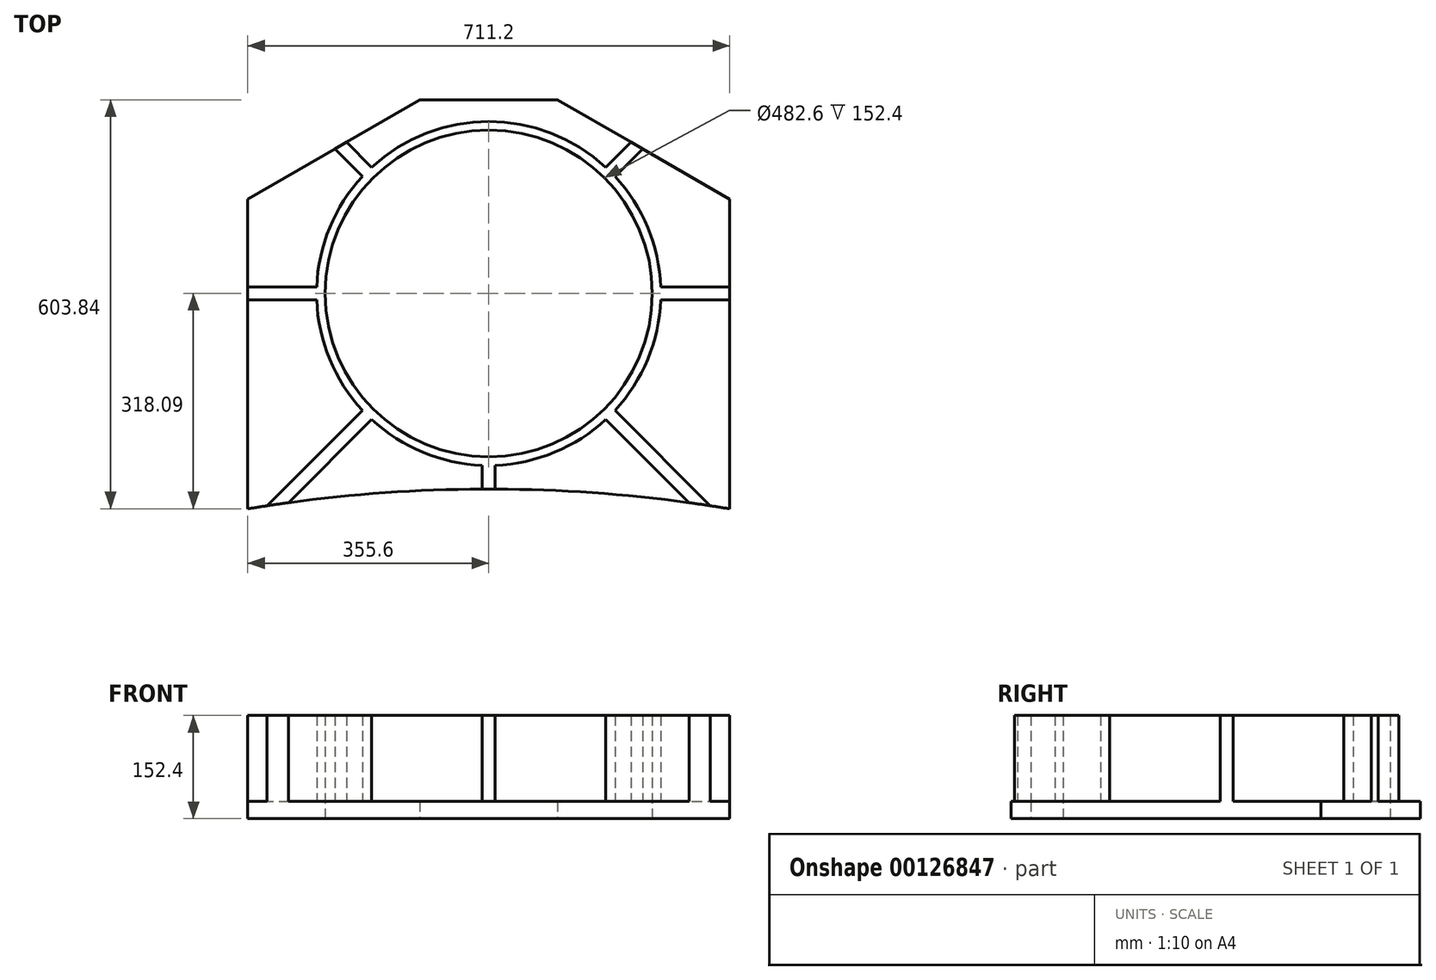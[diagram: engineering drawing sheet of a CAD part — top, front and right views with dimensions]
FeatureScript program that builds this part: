
annotation { "Feature Type Name" : "Feature", "Feature Type Description" : "" }
export const myFeature = defineFeature(function(context is Context, id is Id, definition is map)
    precondition{}
    {
        {
            var Q0;
            Q0=qCreatedBy(makeId("Top.planeOp"),FACE);
            var sketch = newSketch(context, id + "F0", { "sketchPlane" : qUnion([Q0])});
            skLineSegment(sketch, "E0", {"start": v(0, 433.67) * mm, "end": v(0, -509.33) * mm, "construction": true});
            skLineSegment(sketch, "E1", {"start": v(-670.07, 0) * mm, "end": v(724.11, 0) * mm, "construction": true});
            skPoint(sketch, "E2", {"position": v(-101.6, 285.75) * mm});
            skPoint(sketch, "E3", {"position": v(0, 401.5) * mm});
            skPoint(sketch, "E4", {"position": v(101.6, 285.75) * mm});
            skPoint(sketch, "E5", {"position": v(-355.6, 139.1) * mm});
            skPoint(sketch, "E6", {"position": v(355.6, 139.1) * mm});
            skPoint(sketch, "E7", {"position": v(-355.6, -318.09) * mm});
            skArc(sketch, "E8", {"start": v(-355.6, -318.09) * mm, "mid": v(0, -288.92) * mm, "end": v(355.6, -318.09) * mm});
            skLineSegment(sketch, "E9", {"start": v(-355.6, -318.09) * mm, "end": v(-355.6, 139.1) * mm});
            skLineSegment(sketch, "E10", {"start": v(-355.6, 139.1) * mm, "end": v(-101.6, 285.75) * mm});
            skLineSegment(sketch, "E11", {"start": v(-101.6, 285.75) * mm, "end": v(101.6, 285.75) * mm});
            skLineSegment(sketch, "E12", {"start": v(101.6, 285.75) * mm, "end": v(355.6, 139.1) * mm});
            skLineSegment(sketch, "E13", {"start": v(355.6, 139.1) * mm, "end": v(355.6, -318.09) * mm});
            skSolve(sketch);
        }
        {
            var Q0;
            Q0 = qSketchRegion(id + "F0", true);
            extrude(context, id + "F1", {"entities" : qUnion([Q0]), "depth" : 25.4 * mm});
        }
        {
            var Q0;
            Q0=makeQuery(id+"F1.opExtrude","CAP_FACE",FACE,{"disambiguationData":[OSD([sQuery(id+"F0.wireOp",EDGE,"E8"),sQuery(id+"F0.wireOp",EDGE,"E9"),sQuery(id+"F0.wireOp",EDGE,"E10"),sQuery(id+"F0.wireOp",EDGE,"E11"),sQuery(id+"F0.wireOp",EDGE,"E12"),sQuery(id+"F0.wireOp",EDGE,"E13")])],"isStart":false});
            var sketch = newSketch(context, id + "F2", { "sketchPlane" : qUnion([Q0])});
            skLineSegment(sketch, "E14", {"start": v(0, 309.88) * mm, "end": v(0, -342.34) * mm, "construction": true});
            skPoint(sketch, "E14.startSnap0", {"position": v(0, 285.75) * mm});
            skLineSegment(sketch, "E15", {"start": v(-399.29, 0) * mm, "end": v(392.69, 0) * mm, "construction": true});
            skLineSegment(sketch, "E16", {"start": v(-257.96, 257.96) * mm, "end": v(384.23, -384.23) * mm, "construction": true});
            skLineSegment(sketch, "E17", {"start": v(-377.64, -377.64) * mm, "end": v(275.76, 275.76) * mm, "construction": true});
            skLineSegment(sketch, "E18", {"start": v(-226.89, 213.42) * mm, "end": v(-60.2, 46.72) * mm});
            skLineSegment(sketch, "E19", {"start": v(-209.8, 223.28) * mm, "end": v(-46.72, 60.2) * mm});
            skLineSegment(sketch, "E20", {"start": v(-327.03, -313.56) * mm, "end": v(-60.2, -46.72) * mm});
            skLineSegment(sketch, "E21", {"start": v(-295.56, -309.03) * mm, "end": v(-46.72, -60.2) * mm});
            skLineSegment(sketch, "E22", {"start": v(-355.6, 9.52) * mm, "end": v(-75.6, 9.52) * mm});
            skLineSegment(sketch, "E23", {"start": v(-355.6, -9.53) * mm, "end": v(-75.6, -9.53) * mm});
            skLineSegment(sketch, "E24", {"start": v(-355.6, 139.1) * mm, "end": v(-101.6, 285.75) * mm, "construction": true});
            skLineSegment(sketch, "E25", {"start": v(-101.6, 285.75) * mm, "end": v(101.6, 285.75) * mm, "construction": true});
            skLineSegment(sketch, "E26", {"start": v(101.6, 285.75) * mm, "end": v(355.6, 139.1) * mm, "construction": true});
            skLineSegment(sketch, "E27", {"start": v(355.6, 139.1) * mm, "end": v(355.6, -318.09) * mm, "construction": true});
            skLineSegment(sketch, "E28", {"start": v(-355.6, -318.09) * mm, "end": v(-355.6, 139.1) * mm, "construction": true});
            skArc(sketch, "E29", {"start": v(-355.6, -318.09) * mm, "mid": v(0, -288.92) * mm, "end": v(355.6, -318.09) * mm, "construction": true});
            skLineSegment(sketch, "E30", {"start": v(-355.6, -9.53) * mm, "end": v(-355.6, 9.52) * mm});
            skLineSegment(sketch, "E31", {"start": v(-226.89, 213.42) * mm, "end": v(-209.8, 223.28) * mm});
            skLineSegment(sketch, "E32", {"start": v(209.8, 223.28) * mm, "end": v(226.89, 213.42) * mm});
            skLineSegment(sketch, "E33", {"start": v(355.6, 9.53) * mm, "end": v(355.6, -9.52) * mm});
            skArc(sketch, "E34", {"start": v(-327.03, -313.56) * mm, "mid": v(-311.3, -311.24) * mm, "end": v(-295.56, -309.03) * mm});
            skArc(sketch, "E35", {"start": v(295.56, -309.03) * mm, "mid": v(311.3, -311.24) * mm, "end": v(327.03, -313.56) * mm});
            skLineSegment(sketch, "E36", {"start": v(-9.52, -288.95) * mm, "end": v(9.53, -288.95) * mm});
            skCircle(sketch, "E37", {"center": v(0, 0) * mm, "radius": 76.2 * mm, "construction": true});
            skLineSegment(sketch, "E38.trimOffspring", {"start": v(-9.52, -75.6) * mm, "end": v(-9.52, -288.95) * mm});
            skLineSegment(sketch, "E39.trimOffspring", {"start": v(9.53, -75.6) * mm, "end": v(9.53, -288.95) * mm});
            skLineSegment(sketch, "E40.trimOffspring", {"start": v(46.72, -60.2) * mm, "end": v(295.56, -309.03) * mm});
            skLineSegment(sketch, "E41.trimOffspring", {"start": v(60.2, -46.72) * mm, "end": v(327.03, -313.56) * mm});
            skLineSegment(sketch, "E42.trimOffspring", {"start": v(75.6, -9.52) * mm, "end": v(355.6, -9.52) * mm});
            skLineSegment(sketch, "E43.trimOffspring", {"start": v(75.6, 9.53) * mm, "end": v(355.6, 9.53) * mm});
            skLineSegment(sketch, "E44.trimOffspring", {"start": v(60.2, 46.72) * mm, "end": v(226.89, 213.42) * mm});
            skLineSegment(sketch, "E45.trimOffspring", {"start": v(46.72, 60.2) * mm, "end": v(209.8, 223.28) * mm});
            skArc(sketch, "E46", {"start": v(-60.2, 46.72) * mm, "mid": v(-53.88, 53.88) * mm, "end": v(-46.72, 60.2) * mm});
            skArc(sketch, "E47", {"start": v(46.72, 60.2) * mm, "mid": v(53.88, 53.88) * mm, "end": v(60.2, 46.72) * mm});
            skArc(sketch, "E48", {"start": v(75.6, 9.53) * mm, "mid": v(76.2, 0) * mm, "end": v(75.6, -9.52) * mm});
            skArc(sketch, "E49", {"start": v(60.2, -46.72) * mm, "mid": v(53.88, -53.88) * mm, "end": v(46.72, -60.2) * mm});
            skArc(sketch, "E50", {"start": v(9.53, -75.6) * mm, "mid": v(0, -76.2) * mm, "end": v(-9.52, -75.6) * mm});
            skArc(sketch, "E51", {"start": v(-46.72, -60.2) * mm, "mid": v(-53.88, -53.88) * mm, "end": v(-60.2, -46.72) * mm});
            skArc(sketch, "E52", {"start": v(-75.6, -9.52) * mm, "mid": v(-76.2, 0) * mm, "end": v(-75.6, 9.52) * mm});
            skSolve(sketch);
        }
        {
            var Q0;
            Q0 = qSketchRegion(id + "F2", true);
            extrude(context, id + "F3", {"entities" : qUnion([Q0]), "operationType" : NewBodyOperationType.ADD, "depth" : 127 * mm});
        }
        {
            var Q0;
            Q0=makeQuery(id+"F1.opExtrude","CAP_FACE",FACE,{"disambiguationData":[OSD([sQuery(id+"F0.wireOp",EDGE,"E8"),sQuery(id+"F0.wireOp",EDGE,"E9"),sQuery(id+"F0.wireOp",EDGE,"E10"),sQuery(id+"F0.wireOp",EDGE,"E11"),sQuery(id+"F0.wireOp",EDGE,"E12"),sQuery(id+"F0.wireOp",EDGE,"E13")])],"isStart":true});
            var sketch = newSketch(context, id + "F4", { "sketchPlane" : qUnion([Q0])});
            skCircle(sketch, "E53", {"center": v(0, 0) * mm, "radius": 254 * mm});
            skSolve(sketch);
        }
        {
            var Q0;
            Q0 = qSketchRegion(id + "F4", true);
            var Q1;
            Q1=makeQuery(id+"F3.opExtrude","CAP_FACE",FACE,{"disambiguationData":[OSD([sQuery(id+"F2.wireOp",EDGE,"E22"),sQuery(id+"F2.wireOp",EDGE,"E23"),sQuery(id+"F2.wireOp",EDGE,"E30"),sQuery(id+"F2.wireOp",EDGE,"E52")])],"isStart":false});
            extrude(context, id + "F5", {"entities" : qUnion([Q0]), "operationType" : NewBodyOperationType.ADD, "endBound" : BoundingType.UP_TO_SURFACE, "oppositeDirection" : true, "endBoundEntityFace" : qUnion([Q1]), "depth" : 25.4 * mm});
        }
        {
            var Q0;
            Q0=makeQuery(id+"F1.opExtrude","CAP_FACE",FACE,{"disambiguationData":[OSD([sQuery(id+"F0.wireOp",EDGE,"E8"),sQuery(id+"F0.wireOp",EDGE,"E9"),sQuery(id+"F0.wireOp",EDGE,"E10"),sQuery(id+"F0.wireOp",EDGE,"E11"),sQuery(id+"F0.wireOp",EDGE,"E12"),sQuery(id+"F0.wireOp",EDGE,"E13")])],"isStart":true});
            var sketch = newSketch(context, id + "F6", { "sketchPlane" : qUnion([Q0])});
            skCircle(sketch, "E54", {"center": v(0, 0) * mm, "radius": 241.3 * mm});
            skSolve(sketch);
        }
        {
            var Q0;
            Q0 = qSketchRegion(id + "F6", true);
            var Q1;
            {var subQ0=sQuery(id+"F2.wireOp",EDGE,"E52");var subQ1=sQuery(id+"F2.wireOp",EDGE,"E30");var subQ2=sQuery(id+"F2.wireOp",EDGE,"E23");var subQ3=sQuery(id+"F2.wireOp",EDGE,"E22");Q1=makeQuery(id+"F5.boolean.opBoolean","MERGE",FACE,{"derivedFrom":[makeQuery(id+"F3.opExtrude","CAP_FACE",FACE,{"disambiguationData":[OSD([sQuery(id+"F2.wireOp",EDGE,"E18"),sQuery(id+"F2.wireOp",EDGE,"E19"),sQuery(id+"F2.wireOp",EDGE,"E31"),sQuery(id+"F2.wireOp",EDGE,"E46")])],"isStart":false}),makeQuery(id+"F3.opExtrude","CAP_FACE",FACE,{"disambiguationData":[OSD([sQuery(id+"F2.wireOp",EDGE,"E20"),sQuery(id+"F2.wireOp",EDGE,"E21"),sQuery(id+"F2.wireOp",EDGE,"E34"),sQuery(id+"F2.wireOp",EDGE,"E51")])],"isStart":false}),makeQuery(id+"F3.opExtrude","CAP_FACE",FACE,{"disambiguationData":[OSD([subQ3,subQ2,subQ1,subQ0])],"isStart":false}),makeQuery(id+"F3.opExtrude","CAP_FACE",FACE,{"disambiguationData":[OSD([sQuery(id+"F2.wireOp",EDGE,"E32"),sQuery(id+"F2.wireOp",EDGE,"E44.trimOffspring"),sQuery(id+"F2.wireOp",EDGE,"E45.trimOffspring"),sQuery(id+"F2.wireOp",EDGE,"E47")])],"isStart":false}),makeQuery(id+"F3.opExtrude","CAP_FACE",FACE,{"disambiguationData":[OSD([sQuery(id+"F2.wireOp",EDGE,"E33"),sQuery(id+"F2.wireOp",EDGE,"E42.trimOffspring"),sQuery(id+"F2.wireOp",EDGE,"E43.trimOffspring"),sQuery(id+"F2.wireOp",EDGE,"E48")])],"isStart":false}),makeQuery(id+"F3.opExtrude","CAP_FACE",FACE,{"disambiguationData":[OSD([sQuery(id+"F2.wireOp",EDGE,"E35"),sQuery(id+"F2.wireOp",EDGE,"E40.trimOffspring"),sQuery(id+"F2.wireOp",EDGE,"E41.trimOffspring"),sQuery(id+"F2.wireOp",EDGE,"E49")])],"isStart":false}),makeQuery(id+"F3.opExtrude","CAP_FACE",FACE,{"disambiguationData":[OSD([sQuery(id+"F2.wireOp",EDGE,"E36"),sQuery(id+"F2.wireOp",EDGE,"E38.trimOffspring"),sQuery(id+"F2.wireOp",EDGE,"E39.trimOffspring"),sQuery(id+"F2.wireOp",EDGE,"E50")])],"isStart":false}),makeQuery(id+"F5.opExtrude","CAP_FACE",FACE,{"disambiguationData":[OSD([subQ3,subQ2,subQ1,subQ0])],"isStart":false})]});}
            extrude(context, id + "F7", {"entities" : qUnion([Q0]), "operationType" : NewBodyOperationType.REMOVE, "endBound" : BoundingType.UP_TO_SURFACE, "oppositeDirection" : true, "endBoundEntityFace" : qUnion([Q1]), "depth" : 25.4 * mm});
        }
    });
